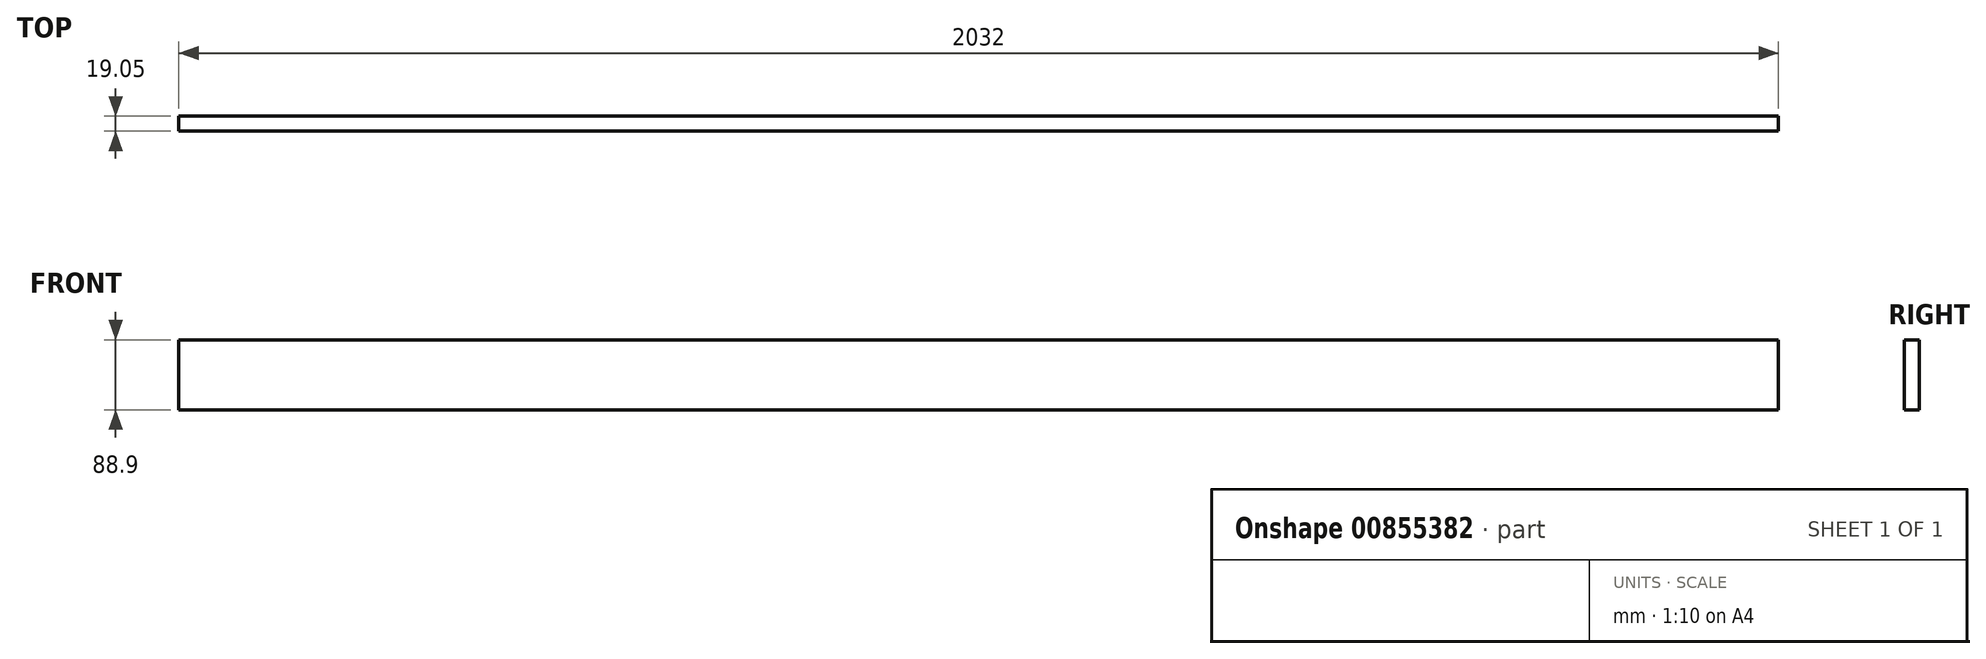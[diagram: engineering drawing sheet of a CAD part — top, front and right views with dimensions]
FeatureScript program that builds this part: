
annotation { "Feature Type Name" : "Feature", "Feature Type Description" : "" }
export const myFeature = defineFeature(function(context is Context, id is Id, definition is map)
    precondition{}
    {
        {
            var Q0;
            Q0=qCreatedBy(makeId("Right.planeOp"),FACE);
            var sketch = newSketch(context, id + "F0", { "sketchPlane" : qUnion([Q0])});
            skLineSegment(sketch, "E0.bottom", {"start": v(0, 0) * mm, "end": v(-19.05, 0) * mm});
            skLineSegment(sketch, "E0.top", {"start": v(0, 88.9) * mm, "end": v(-19.05, 88.9) * mm});
            skLineSegment(sketch, "E0.left", {"start": v(0, 0) * mm, "end": v(0, 88.9) * mm});
            skLineSegment(sketch, "E0.right", {"start": v(-19.05, 0) * mm, "end": v(-19.05, 88.9) * mm});
            skSolve(sketch);
        }
        {
            var Q0;
            Q0 = qSketchRegion(id + "F0", true);
            extrude(context, id + "F1", {"entities" : qUnion([Q0]), "depth" : 2032 * mm, "offsetDistance" : 25.4 * mm});
        }
    });
